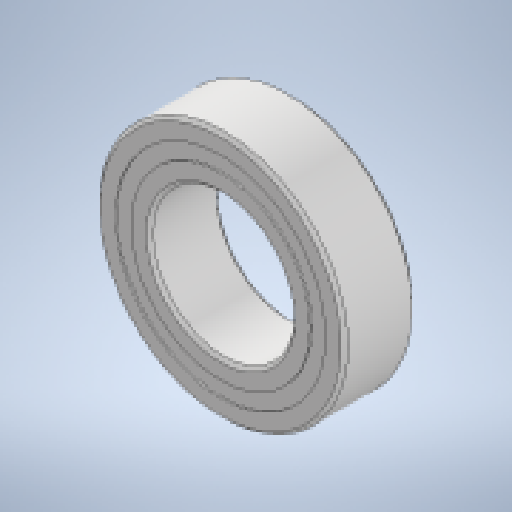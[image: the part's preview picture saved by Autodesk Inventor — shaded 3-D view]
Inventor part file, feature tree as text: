
AUTODESK INVENTOR PART (.ipt)
format: ipt  version: 2023 (Build 270158030, 158C)  size: 618,496 bytes
history: native  units: in
note: dims shown in document units (in); Inventor stores cm internally (conversion verified against a paired STEP export)
features: other x11, revolve x5
ambient origin geometry x8: Origin, YZ Plane, XZ Plane, XY Plane, X Axis, Y Axis, Z Axis, Center Point
bodies: Solid1 (feature_tree), Solid2 (feature_tree), Solid3 (feature_tree), Solid4 (feature_tree), Solid5 (feature_tree), Solid6 (feature_tree), Solid7 (feature_tree), Solid8 (feature_tree), Solid9 (feature_tree), Solid10 (feature_tree), Solid11 (feature_tree), Solid12 (feature_tree), Solid13 (feature_tree), Solid14 (feature_tree), Solid15 (feature_tree), Solid16 (feature_tree)
feature tree (16):
  revolve  "Revolve1"  [1 undecoded]
  revolve  "Revolve3"  [1 undecoded]
  revolve  "Revolve4"  [1 undecoded]
  other  "CirPattern1[1]"
  other  "CirPattern1[2]"
  other  "CirPattern1[3]"
  other  "CirPattern1[4]"
  other  "CirPattern1[5]"
  other  "CirPattern1[6]"
  other  "CirPattern1[7]"
  other  "CirPattern1[8]"
  other  "CirPattern1[9]"
  other  "CirPattern1[10]"
  other  "CirPattern1[11]"
  revolve  "Revolve5[1]"  [1 undecoded]
  revolve  "Revolve5[2]"  [1 undecoded]
note: 5 required parameter values undecoded (feature->parameter linkage not recoverable at this tier; creation-order binding heuristic only, values carry confidence <= 0.55)
